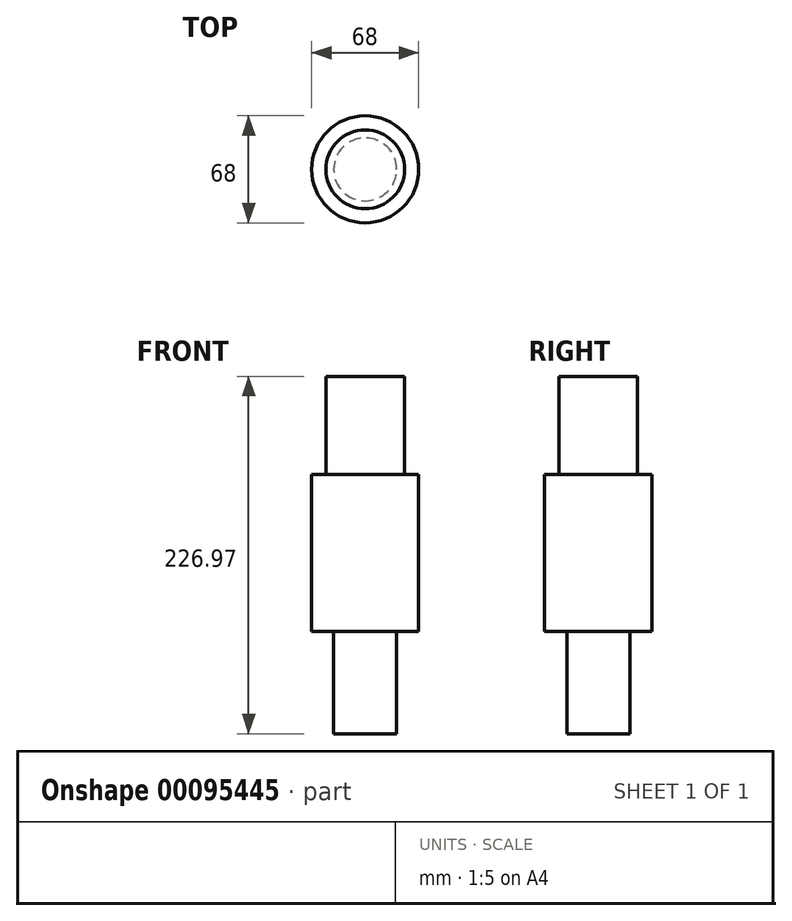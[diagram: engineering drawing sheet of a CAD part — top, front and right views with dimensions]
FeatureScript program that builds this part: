
annotation { "Feature Type Name" : "Feature", "Feature Type Description" : "" }
export const myFeature = defineFeature(function(context is Context, id is Id, definition is map)
    precondition{}
    {
        {
            var Q0;
            Q0=qCreatedBy(makeId("Front.planeOp"),FACE);
            var sketch = newSketch(context, id + "F0", { "sketchPlane" : qUnion([Q0])});
            skLineSegment(sketch, "E0", {"start": v(0, 161.97) * mm, "end": v(-25, 161.97) * mm});
            skLineSegment(sketch, "E1", {"start": v(-25, 161.97) * mm, "end": v(-25, 99.5) * mm});
            skLineSegment(sketch, "E2", {"start": v(-25, 99.5) * mm, "end": v(-34, 99.5) * mm});
            skLineSegment(sketch, "E3", {"start": v(-34, 99.5) * mm, "end": v(-34, 0) * mm});
            skLineSegment(sketch, "E4", {"start": v(-34, 0) * mm, "end": v(-20, 0) * mm});
            skLineSegment(sketch, "E5", {"start": v(-20, 0) * mm, "end": v(-20, -65) * mm});
            skLineSegment(sketch, "E6", {"start": v(-20, -65) * mm, "end": v(0, -65) * mm});
            skLineSegment(sketch, "E7", {"start": v(0, -65) * mm, "end": v(0, 161.97) * mm});
            skSolve(sketch);
        }
        {
            var Q0;
            Q0=makeQuery(id+"F0.imprint","IMPRINT",FACE,{"disambiguationData":[TD([[makeQuery(id+"F0.imprint","IMPRINT",EDGE,{"derivedFrom":sQuery(id+"F0.wireOp",EDGE,"E0")}),1.0]])]});
            var Q1;
            Q1=sQuery(id+"F0.wireOp",EDGE,"E7");
            revolve(context, id + "F1", {"entities" : qUnion([Q0]), "axis" : qUnion([Q1]), "revolveType" : RevolveType.FULL});
        }
    });
